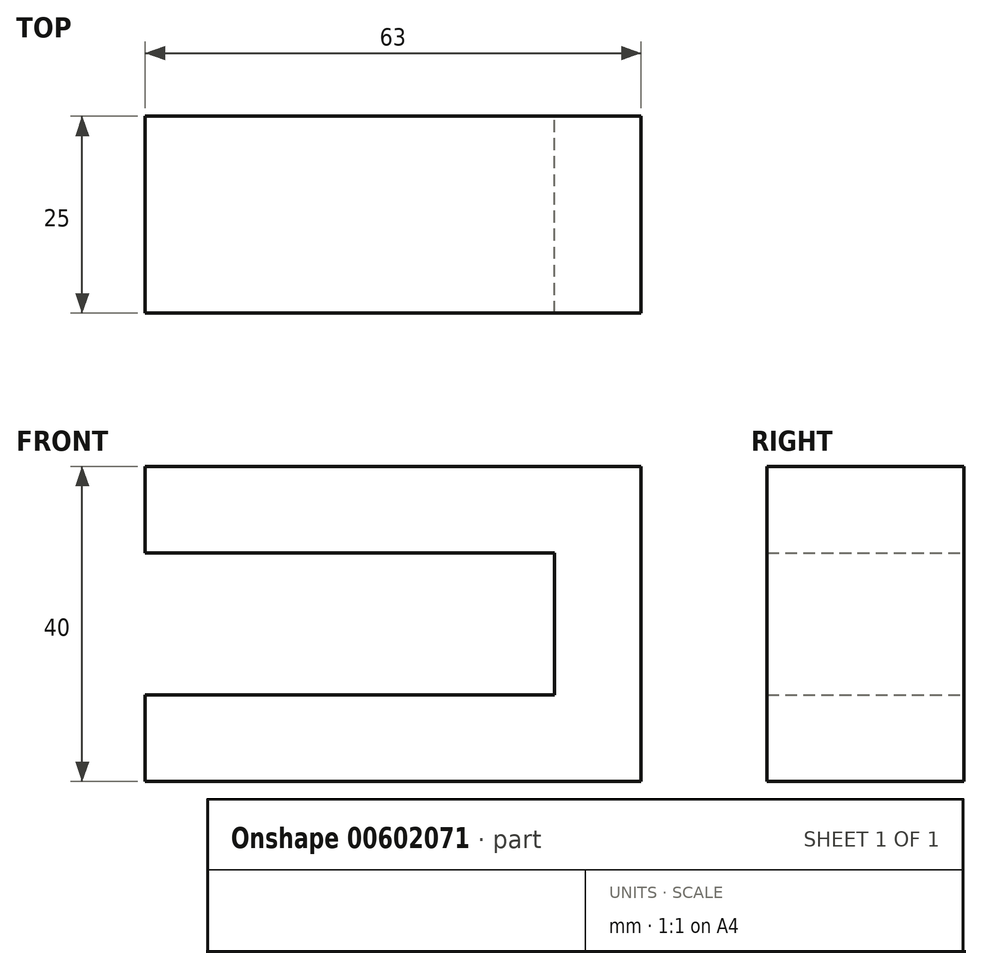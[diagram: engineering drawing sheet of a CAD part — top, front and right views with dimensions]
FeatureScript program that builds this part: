
annotation { "Feature Type Name" : "Feature", "Feature Type Description" : "" }
export const myFeature = defineFeature(function(context is Context, id is Id, definition is map)
    precondition{}
    {
        {
            var Q0;
            Q0=qCreatedBy(makeId("Front.planeOp"),FACE);
            var sketch = newSketch(context, id + "F0", { "sketchPlane" : qUnion([Q0])});
            skLineSegment(sketch, "E0", {"start": v(55.16, 46.74) * mm, "end": v(66.16, 46.74) * mm});
            skLineSegment(sketch, "E1", {"start": v(66.16, 46.74) * mm, "end": v(66.16, 6.74) * mm});
            skLineSegment(sketch, "E2", {"start": v(66.16, 6.74) * mm, "end": v(55.16, 6.74) * mm});
            skLineSegment(sketch, "E3", {"start": v(55.16, 6.74) * mm, "end": v(55.16, 46.74) * mm});
            skLineSegment(sketch, "E4", {"start": v(55.16, 46.74) * mm, "end": v(3.16, 46.74) * mm});
            skLineSegment(sketch, "E5", {"start": v(3.16, 46.74) * mm, "end": v(3.16, 35.74) * mm});
            skLineSegment(sketch, "E6", {"start": v(3.16, 35.74) * mm, "end": v(55.16, 35.74) * mm});
            skLineSegment(sketch, "E7", {"start": v(55.16, 35.74) * mm, "end": v(55.16, 6.74) * mm});
            skLineSegment(sketch, "E8", {"start": v(3.16, 6.74) * mm, "end": v(3.16, 17.74) * mm});
            skLineSegment(sketch, "E9", {"start": v(3.16, 17.74) * mm, "end": v(55.16, 17.74) * mm});
            skLineSegment(sketch, "E10", {"start": v(55.16, 17.74) * mm, "end": v(55.16, 6.74) * mm});
            skLineSegment(sketch, "E11", {"start": v(55.16, 6.74) * mm, "end": v(3.16, 6.74) * mm});
            skSolve(sketch);
        }
        {
            var Q0;
            Q0=makeQuery(id+"F0.imprint","IMPRINT",FACE,{"disambiguationData":[TD([[makeQuery(id+"F0.imprint","IMPRINT",EDGE,{"derivedFrom":sQuery(id+"F0.wireOp",EDGE,"E3")}),1.0]])]});
            var Q1;
            Q1=makeQuery(id+"F0.imprint","IMPRINT",FACE,{"disambiguationData":[TD([[makeQuery(id+"F0.imprint","IMPRINT",EDGE,{"derivedFrom":sQuery(id+"F0.wireOp",EDGE,"E8")}),-1.0]])]});
            var Q2;
            Q2=makeQuery(id+"F0.imprint","IMPRINT",FACE,{"disambiguationData":[TD([[makeQuery(id+"F0.imprint","IMPRINT",EDGE,{"derivedFrom":sQuery(id+"F0.wireOp",EDGE,"E0")}),-1.0]])]});
            extrude(context, id + "F1", {"entities" : qUnion([Q0, Q1, Q2]), "depth" : 25 * mm, "offsetDistance" : 25 * mm});
        }
    });
